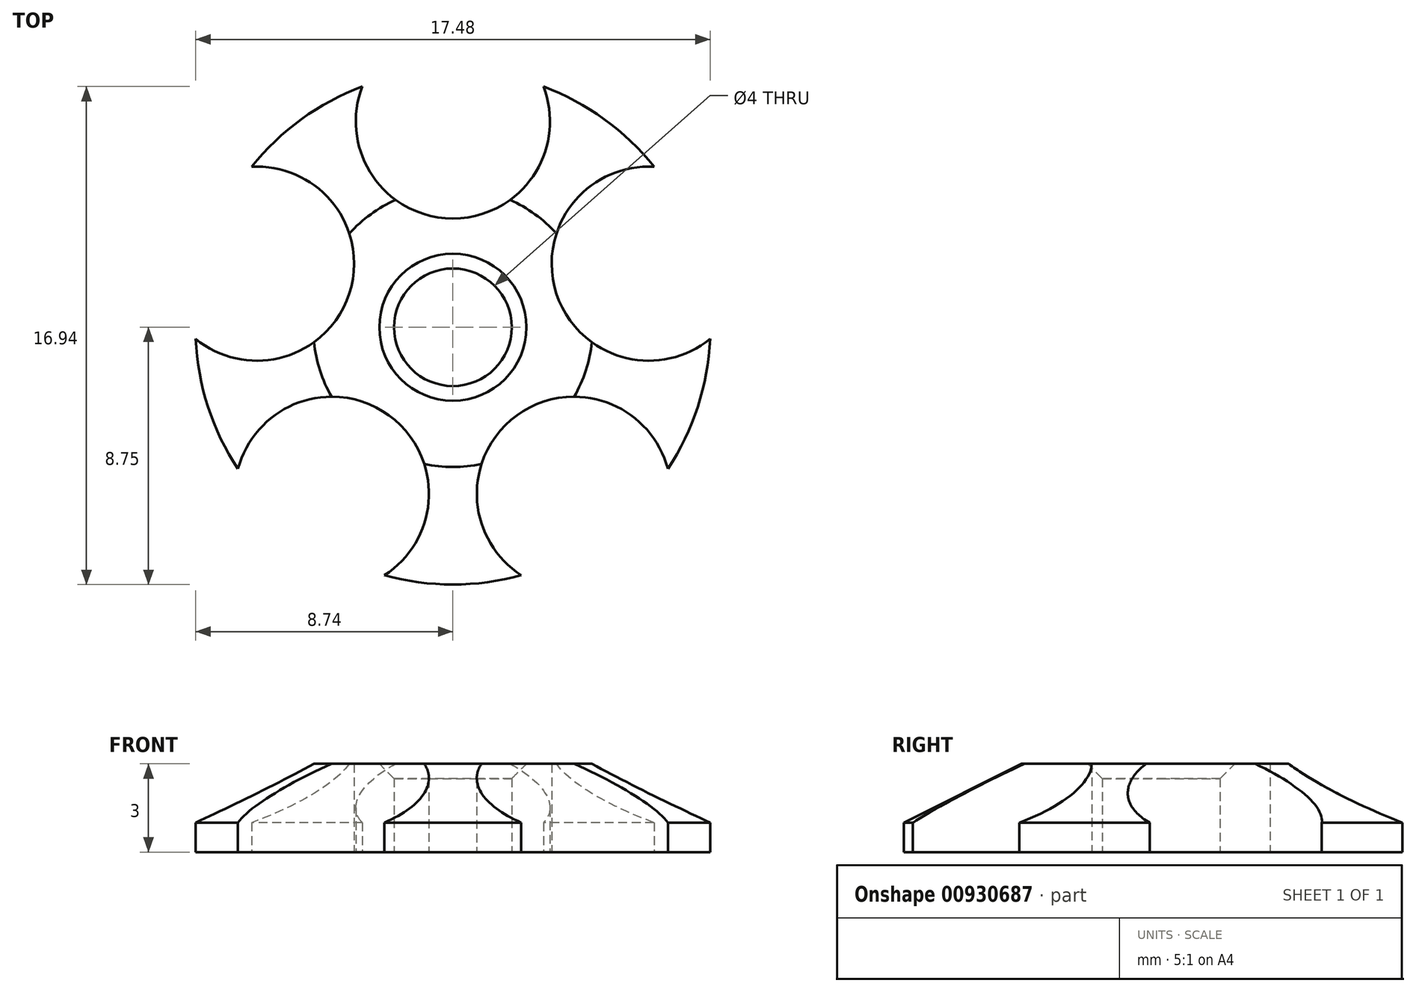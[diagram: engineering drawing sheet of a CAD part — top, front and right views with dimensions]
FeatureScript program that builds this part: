
annotation { "Feature Type Name" : "Feature", "Feature Type Description" : "" }
export const myFeature = defineFeature(function(context is Context, id is Id, definition is map)
    precondition{}
    {
        {
            var Q0;
            Q0=qCreatedBy(makeId("Top.planeOp"),FACE);
            var sketch = newSketch(context, id + "F0", { "sketchPlane" : qUnion([Q0])});
            skArc(sketch, "E0", {"start": v(-8.74, -0.4) * mm, "mid": v(-8.32, -2.7) * mm, "end": v(-7.3, -4.82) * mm});
            skCircle(sketch, "E1", {"center": v(0, 0) * mm, "radius": 7 * mm, "construction": true});
            skLineSegment(sketch, "E2", {"start": v(0, 0) * mm, "end": v(0, 8.75) * mm, "construction": true});
            skLineSegment(sketch, "E3", {"start": v(0, 0) * mm, "end": v(-8.32, 2.7) * mm, "construction": true});
            skLineSegment(sketch, "E4", {"start": v(0, 0) * mm, "end": v(8.32, 2.7) * mm, "construction": true});
            skLineSegment(sketch, "E5", {"start": v(0, 0) * mm, "end": v(-5.14, -7.08) * mm, "construction": true});
            skLineSegment(sketch, "E6", {"start": v(0, 0) * mm, "end": v(5.14, -7.08) * mm, "construction": true});
            skCircle(sketch, "E7", {"center": v(-6.66, 2.16) * mm, "radius": 1.75 * mm, "construction": true});
            skCircle(sketch, "E8", {"center": v(0, 7) * mm, "radius": 1.75 * mm, "construction": true});
            skCircle(sketch, "E9", {"center": v(6.66, 2.16) * mm, "radius": 1.75 * mm, "construction": true});
            skCircle(sketch, "E10", {"center": v(4.11, -5.66) * mm, "radius": 1.75 * mm, "construction": true});
            skCircle(sketch, "E11", {"center": v(-4.11, -5.66) * mm, "radius": 1.75 * mm, "construction": true});
            skArc(sketch, "E12", {"start": v(-8.74, -0.4) * mm, "mid": v(-3.52, 1.14) * mm, "end": v(-6.84, 5.46) * mm});
            skArc(sketch, "E13", {"start": v(-3.08, 8.2) * mm, "mid": v(0, 3.7) * mm, "end": v(3.08, 8.2) * mm});
            skArc(sketch, "E14", {"start": v(6.84, 5.46) * mm, "mid": v(3.52, 1.14) * mm, "end": v(8.74, -0.4) * mm});
            skArc(sketch, "E15", {"start": v(7.3, -4.82) * mm, "mid": v(2.17, -3) * mm, "end": v(2.32, -8.44) * mm});
            skArc(sketch, "E16", {"start": v(-2.32, -8.44) * mm, "mid": v(-2.17, -3) * mm, "end": v(-7.3, -4.82) * mm});
            skArc(sketch, "E17.trimOffspring", {"start": v(-3.08, 8.2) * mm, "mid": v(-5.14, 7.08) * mm, "end": v(-6.84, 5.46) * mm});
            skArc(sketch, "E18.trimOffspring", {"start": v(6.84, 5.46) * mm, "mid": v(5.14, 7.08) * mm, "end": v(3.08, 8.2) * mm});
            skArc(sketch, "E19.trimOffspring", {"start": v(-2.32, -8.44) * mm, "mid": v(0, -8.75) * mm, "end": v(2.32, -8.44) * mm});
            skArc(sketch, "E20.trimOffspring", {"start": v(7.3, -4.82) * mm, "mid": v(8.32, -2.7) * mm, "end": v(8.74, -0.4) * mm});
            skCircle(sketch, "E21", {"center": v(0, 0) * mm, "radius": 2 * mm});
            skSolve(sketch);
        }
        {
            var Q0;
            Q0=qSketchRegion(id+"F0",true);
            extrude(context, id + "F1", {"entities" : qUnion([Q0]), "depth" : 3 * mm});
        }
        {
            var Q0;
            Q0=makeQuery(id+"F1.opExtrude","CAP_EDGE",EDGE,{"disambiguationData":[OSD([sQuery(id+"F0.wireOp",EDGE,"E0")])],"isStart":false});
            var Q1;
            Q1=makeQuery(id+"F1.opExtrude","CAP_EDGE",EDGE,{"disambiguationData":[OSD([sQuery(id+"F0.wireOp",EDGE,"E19.trimOffspring")])],"isStart":false});
            var Q2;
            Q2=makeQuery(id+"F1.opExtrude","CAP_EDGE",EDGE,{"disambiguationData":[OSD([sQuery(id+"F0.wireOp",EDGE,"E20.trimOffspring")])],"isStart":false});
            var Q3;
            Q3=makeQuery(id+"F1.opExtrude","CAP_EDGE",EDGE,{"disambiguationData":[OSD([sQuery(id+"F0.wireOp",EDGE,"E18.trimOffspring")])],"isStart":false});
            var Q4;
            Q4=makeQuery(id+"F1.opExtrude","CAP_EDGE",EDGE,{"disambiguationData":[OSD([sQuery(id+"F0.wireOp",EDGE,"E17.trimOffspring")])],"isStart":false});
            chamfer(context, id + "F2", {"entities" : qUnion([Q0, Q1, Q2, Q3, Q4]), "chamferType" : ChamferType.TWO_OFFSETS, "width1" : 4 * mm, "oppositeDirection" : false, "width2" : 2 * mm, "tangentPropagation" : true});
        }
        {
            var Q0;
            Q0=makeQuery(id+"F1.opExtrude","CAP_EDGE",EDGE,{"disambiguationData":[OSD([sQuery(id+"F0.wireOp",EDGE,"E21")])],"isStart":false});
            chamfer(context, id + "F3", {"entities" : qUnion([Q0]), "width" : 0.5 * mm, "tangentPropagation" : true});
        }
    });
